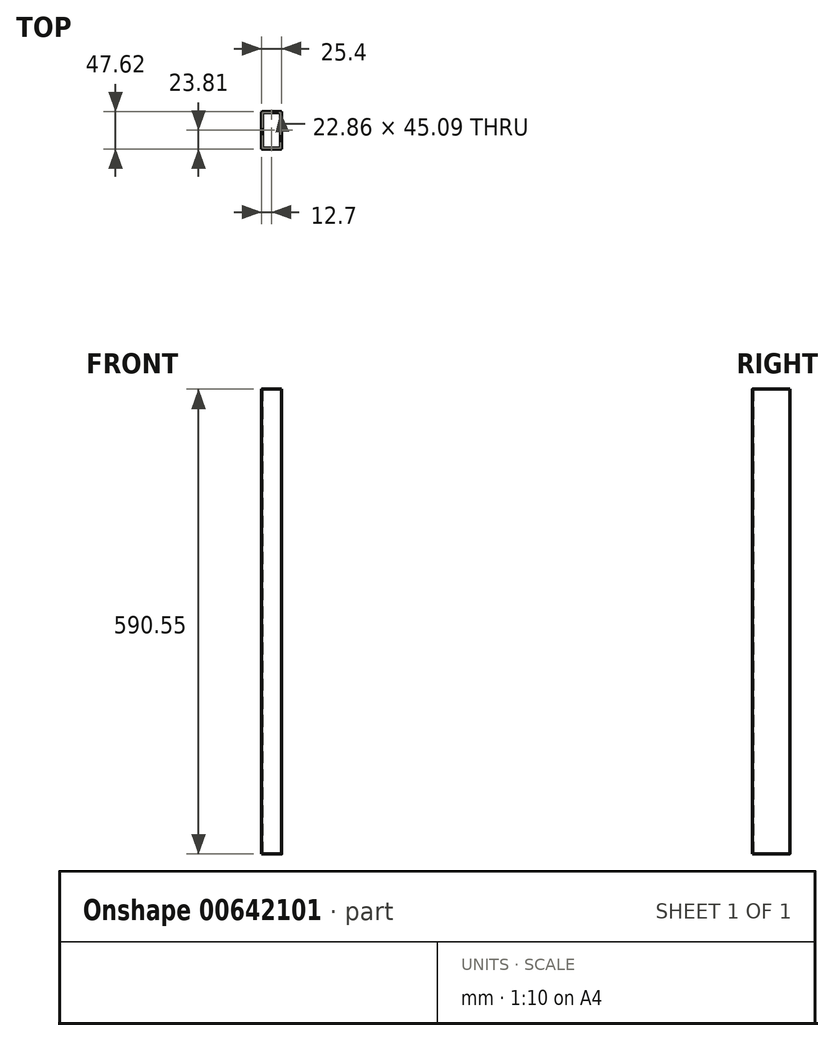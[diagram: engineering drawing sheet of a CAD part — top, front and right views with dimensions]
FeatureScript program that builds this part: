
annotation { "Feature Type Name" : "Feature", "Feature Type Description" : "" }
export const myFeature = defineFeature(function(context is Context, id is Id, definition is map)
    precondition{}
    {
        {
            var Q0;
            Q0=qCreatedBy(makeId("Top.planeOp"),FACE);
            var sketch = newSketch(context, id + "F0", { "sketchPlane" : qUnion([Q0])});
            skLineSegment(sketch, "E0.bottom", {"start": v(12.07, -23.81) * mm, "end": v(-12.07, -23.81) * mm});
            skLineSegment(sketch, "E0.top", {"start": v(12.06, 23.81) * mm, "end": v(-11.43, 23.81) * mm});
            skLineSegment(sketch, "E0.left", {"start": v(12.7, -23.18) * mm, "end": v(12.7, 23.18) * mm});
            skLineSegment(sketch, "E0.right", {"start": v(-12.7, -23.18) * mm, "end": v(-12.7, 22.54) * mm});
            skPoint(sketch, "E0.middle", {"position": v(0, 0) * mm});
            skPoint(sketch, "E1.visualSharp", {"position": v(-12.7, 23.81) * mm});
            skArc(sketch, "E1.filletArc", {"start": v(-11.43, 23.81) * mm, "mid": v(-12.33, 23.44) * mm, "end": v(-12.7, 22.54) * mm});
            skPoint(sketch, "E2.visualSharp", {"position": v(12.7, 23.81) * mm});
            skArc(sketch, "E2.filletArc", {"start": v(12.7, 23.18) * mm, "mid": v(12.51, 23.63) * mm, "end": v(12.06, 23.81) * mm});
            skPoint(sketch, "E3.visualSharp", {"position": v(-12.7, -23.81) * mm});
            skArc(sketch, "E3.filletArc", {"start": v(-12.7, -23.18) * mm, "mid": v(-12.51, -23.63) * mm, "end": v(-12.07, -23.81) * mm});
            skPoint(sketch, "E4.visualSharp", {"position": v(12.7, -23.81) * mm});
            skArc(sketch, "E4.filletArc", {"start": v(12.07, -23.81) * mm, "mid": v(12.51, -23.63) * mm, "end": v(12.7, -23.18) * mm});
            skLineSegment(sketch, "E5.bottom", {"start": v(-11.43, 22.54) * mm, "end": v(11.43, 22.54) * mm});
            skLineSegment(sketch, "E5.top", {"start": v(-11.43, -22.54) * mm, "end": v(11.43, -22.54) * mm});
            skLineSegment(sketch, "E5.left", {"start": v(-11.43, 22.54) * mm, "end": v(-11.43, -22.54) * mm});
            skLineSegment(sketch, "E5.right", {"start": v(11.43, 22.54) * mm, "end": v(11.43, -22.54) * mm});
            skSolve(sketch);
        }
        {
            var Q0;
            Q0=makeQuery(id+"F0.imprint","IMPRINT",FACE,{"disambiguationData":[TD([[makeQuery(id+"F0.imprint","IMPRINT",EDGE,{"derivedFrom":sQuery(id+"F0.wireOp",EDGE,"E0.bottom")}),-1.0]])]});
            extrude(context, id + "F1", {"entities" : qUnion([Q0]), "depth" : 590.55 * mm, "offsetDistance" : 25.4 * mm});
        }
    });
